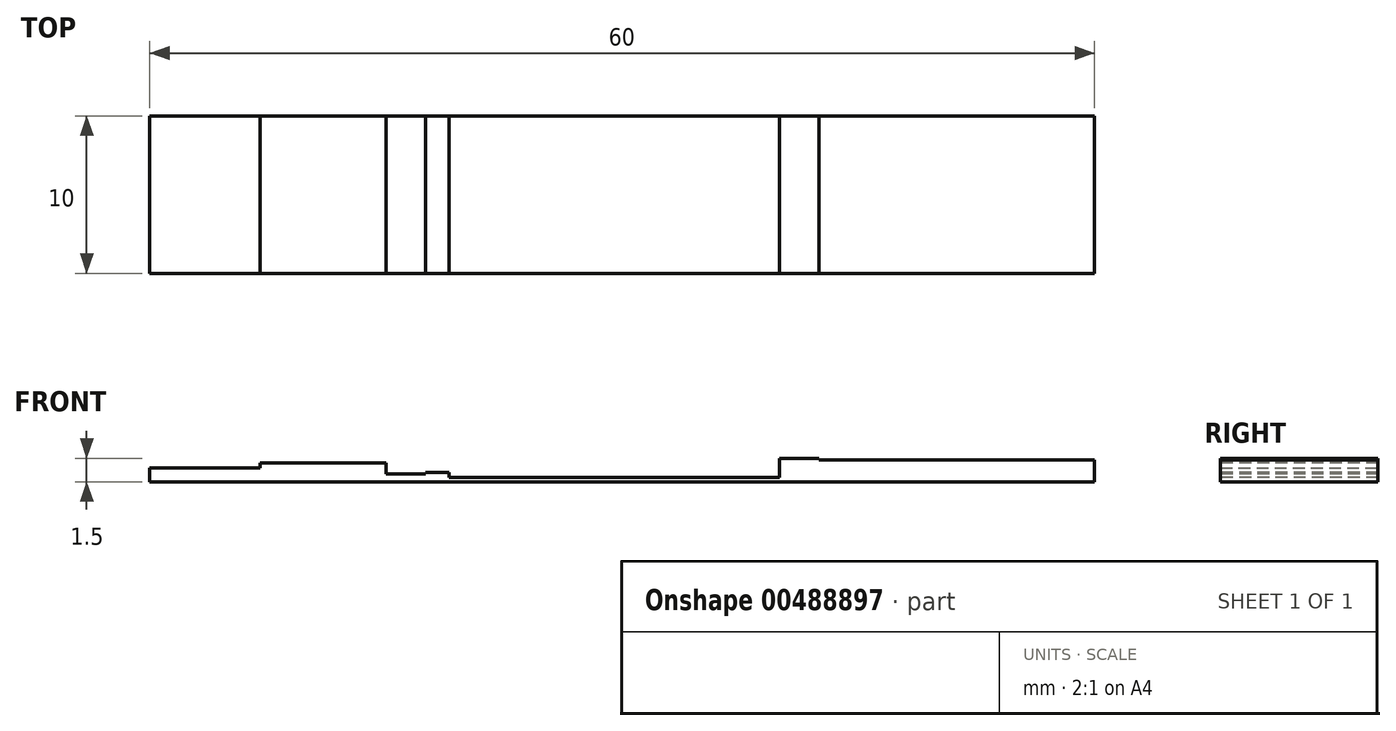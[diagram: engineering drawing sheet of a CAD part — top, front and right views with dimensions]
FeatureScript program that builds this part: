
annotation { "Feature Type Name" : "Feature", "Feature Type Description" : "" }
export const myFeature = defineFeature(function(context is Context, id is Id, definition is map)
    precondition{}
    {
        {
            var Q0;
            Q0=qCreatedBy(makeId("Top.planeOp"),FACE);
            var sketch = newSketch(context, id + "F0", { "sketchPlane" : qUnion([Q0])});
            skLineSegment(sketch, "E0.bottom", {"start": v(30, -5) * mm, "end": v(-30, -5) * mm});
            skLineSegment(sketch, "E0.top", {"start": v(30, 5) * mm, "end": v(-30, 5) * mm});
            skLineSegment(sketch, "E0.left", {"start": v(30, -5) * mm, "end": v(30, 5) * mm});
            skLineSegment(sketch, "E0.right", {"start": v(-30, -5) * mm, "end": v(-30, 5) * mm});
            skPoint(sketch, "E0.middle", {"position": v(0, 0) * mm});
            skSolve(sketch);
        }
        {
            var Q0;
            Q0=makeQuery(id+"F0.imprint","IMPRINT",FACE,{"disambiguationData":[TD([[makeQuery(id+"F0.imprint","IMPRINT",EDGE,{"derivedFrom":sQuery(id+"F0.wireOp",EDGE,"E0.bottom")}),-1.0]])]});
            extrude(context, id + "F1", {"entities" : qUnion([Q0]), "depth" : 0.2 * mm});
        }
        {
            var Q0;
            Q0=makeQuery(id+"F1.opExtrude","CAP_FACE",FACE,{"disambiguationData":[OSD([sQuery(id+"F0.wireOp",EDGE,"E0.bottom"),sQuery(id+"F0.wireOp",EDGE,"E0.top"),sQuery(id+"F0.wireOp",EDGE,"E0.left"),sQuery(id+"F0.wireOp",EDGE,"E0.right")])],"isStart":false});
            var sketch = newSketch(context, id + "F2", { "sketchPlane" : qUnion([Q0])});
            skLineSegment(sketch, "E1.bottom", {"start": v(-12.5, 5) * mm, "end": v(12.5, 5) * mm});
            skLineSegment(sketch, "E1.top", {"start": v(-12.5, -5) * mm, "end": v(12.5, -5) * mm});
            skLineSegment(sketch, "E1.left", {"start": v(-12.5, 5) * mm, "end": v(-12.5, -5) * mm});
            skLineSegment(sketch, "E1.right", {"start": v(12.5, 5) * mm, "end": v(12.5, -5) * mm});
            skSolve(sketch);
        }
        {
            var Q0;
            Q0=makeQuery(id+"F2.imprint","IMPRINT",FACE,{"disambiguationData":[TD([[makeQuery(id+"F2.imprint","IMPRINT",EDGE,{"derivedFrom":sQuery(id+"F2.wireOp",EDGE,"E1.bottom")}),1.0]])]});
            extrude(context, id + "F3", {"entities" : qUnion([Q0]), "operationType" : NewBodyOperationType.ADD, "depth" : 0.1 * mm});
        }
        {
            var Q0;
            Q0=makeQuery(id+"F3.opExtrude","CAP_FACE",FACE,{"disambiguationData":[OSD([sQuery(id+"F2.wireOp",EDGE,"E1.bottom"),sQuery(id+"F2.wireOp",EDGE,"E1.top"),sQuery(id+"F2.wireOp",EDGE,"E1.left"),sQuery(id+"F2.wireOp",EDGE,"E1.right")])],"isStart":false});
            var sketch = newSketch(context, id + "F4", { "sketchPlane" : qUnion([Q0])});
            skLineSegment(sketch, "E2.bottom", {"start": v(-12.5, 5) * mm, "end": v(-11, 5) * mm});
            skLineSegment(sketch, "E2.top", {"start": v(-12.5, -5) * mm, "end": v(-11, -5) * mm});
            skLineSegment(sketch, "E2.left", {"start": v(-12.5, 5) * mm, "end": v(-12.5, -5) * mm});
            skLineSegment(sketch, "E2.right", {"start": v(-11, 5) * mm, "end": v(-11, -5) * mm});
            skSolve(sketch);
        }
        {
            var Q0;
            Q0=makeQuery(id+"F4.imprint","IMPRINT",FACE,{"disambiguationData":[TD([[makeQuery(id+"F4.imprint","IMPRINT",EDGE,{"derivedFrom":sQuery(id+"F4.wireOp",EDGE,"E2.bottom")}),1.0]])]});
            extrude(context, id + "F5", {"entities" : qUnion([Q0]), "operationType" : NewBodyOperationType.ADD, "depth" : 0.3 * mm});
        }
        {
            var Q0;
            {var subQ0=sQuery(id+"F0.wireOp",EDGE,"E0.top");var subQ1=sQuery(id+"F0.wireOp",EDGE,"E0.right");var subQ2=sQuery(id+"F0.wireOp",EDGE,"E0.bottom");Q0=makeQuery(id+"F3.boolean.opBoolean","SPLIT",FACE,{"disambiguationData":[TD([makeQuery(id+"F1.opExtrude","SWEPT_FACE",FACE,{"disambiguationData":[OSD([subQ1])]})])],"derivedFrom":makeQuery(id+"F1.opExtrude","CAP_FACE",FACE,{"disambiguationData":[OSD([subQ2,subQ0,sQuery(id+"F0.wireOp",EDGE,"E0.left"),subQ1])],"isStart":false})});}
            var sketch = newSketch(context, id + "F6", { "sketchPlane" : qUnion([Q0])});
            skLineSegment(sketch, "E3.bottom", {"start": v(-12.5, 5) * mm, "end": v(-23, 5) * mm});
            skLineSegment(sketch, "E3.top", {"start": v(-12.5, -5) * mm, "end": v(-23, -5) * mm});
            skLineSegment(sketch, "E3.left", {"start": v(-12.5, 5) * mm, "end": v(-12.5, -5) * mm});
            skLineSegment(sketch, "E3.right", {"start": v(-23, 5) * mm, "end": v(-23, -5) * mm});
            skSolve(sketch);
        }
        {
            var Q0;
            Q0=makeQuery(id+"F6.imprint","IMPRINT",FACE,{"disambiguationData":[TD([[makeQuery(id+"F6.imprint","IMPRINT",EDGE,{"derivedFrom":sQuery(id+"F6.wireOp",EDGE,"E3.bottom")}),1.0]])]});
            extrude(context, id + "F7", {"entities" : qUnion([Q0]), "operationType" : NewBodyOperationType.ADD, "depth" : 0.3 * mm});
        }
        {
            var Q0;
            {var subQ0=sQuery(id+"F0.wireOp",EDGE,"E0.top");var subQ1=sQuery(id+"F0.wireOp",EDGE,"E0.right");var subQ2=sQuery(id+"F0.wireOp",EDGE,"E0.bottom");Q0=makeQuery(id+"F3.boolean.opBoolean","SPLIT",FACE,{"disambiguationData":[TD([makeQuery(id+"F1.opExtrude","SWEPT_FACE",FACE,{"disambiguationData":[OSD([subQ1])]})])],"derivedFrom":makeQuery(id+"F1.opExtrude","CAP_FACE",FACE,{"disambiguationData":[OSD([subQ2,subQ0,sQuery(id+"F0.wireOp",EDGE,"E0.left"),subQ1])],"isStart":false})});}
            var sketch = newSketch(context, id + "F8", { "sketchPlane" : qUnion([Q0])});
            skLineSegment(sketch, "E4.bottom", {"start": v(-23, 5) * mm, "end": v(-30, 5) * mm});
            skLineSegment(sketch, "E4.top", {"start": v(-23, -5) * mm, "end": v(-30, -5) * mm});
            skLineSegment(sketch, "E4.left", {"start": v(-23, 5) * mm, "end": v(-23, -5) * mm});
            skLineSegment(sketch, "E4.right", {"start": v(-30, 5) * mm, "end": v(-30, -5) * mm});
            skSolve(sketch);
        }
        {
            var Q0;
            Q0=makeQuery(id+"F8.imprint","IMPRINT",FACE,{"disambiguationData":[TD([[makeQuery(id+"F8.imprint","IMPRINT",EDGE,{"derivedFrom":sQuery(id+"F8.wireOp",EDGE,"E4.bottom")}),1.0]])]});
            extrude(context, id + "F9", {"entities" : qUnion([Q0]), "operationType" : NewBodyOperationType.ADD, "depth" : 0.7 * mm});
        }
        {
            var Q0;
            Q0=makeQuery(id+"F7.opExtrude","CAP_FACE",FACE,{"disambiguationData":[OSD([sQuery(id+"F6.wireOp",EDGE,"E3.bottom"),sQuery(id+"F6.wireOp",EDGE,"E3.top"),sQuery(id+"F6.wireOp",EDGE,"E3.left"),sQuery(id+"F6.wireOp",EDGE,"E3.right")])],"isStart":false});
            var sketch = newSketch(context, id + "F10", { "sketchPlane" : qUnion([Q0])});
            skLineSegment(sketch, "E5.bottom", {"start": v(-23, 5) * mm, "end": v(-15, 5) * mm});
            skLineSegment(sketch, "E5.top", {"start": v(-23, -5) * mm, "end": v(-15, -5) * mm});
            skLineSegment(sketch, "E5.left", {"start": v(-23, 5) * mm, "end": v(-23, -5) * mm});
            skLineSegment(sketch, "E5.right", {"start": v(-15, 5) * mm, "end": v(-15, -5) * mm});
            skSolve(sketch);
        }
        {
            var Q0;
            Q0=makeQuery(id+"F10.imprint","IMPRINT",FACE,{"disambiguationData":[TD([[makeQuery(id+"F10.imprint","IMPRINT",EDGE,{"derivedFrom":sQuery(id+"F10.wireOp",EDGE,"E5.bottom")}),1.0]])]});
            extrude(context, id + "F11", {"entities" : qUnion([Q0]), "operationType" : NewBodyOperationType.ADD, "depth" : 0.7 * mm});
        }
        {
            var Q0;
            {var subQ0=sQuery(id+"F0.wireOp",EDGE,"E0.left");var subQ1=sQuery(id+"F0.wireOp",EDGE,"E0.top");var subQ2=sQuery(id+"F0.wireOp",EDGE,"E0.bottom");Q0=makeQuery(id+"F3.boolean.opBoolean","SPLIT",FACE,{"disambiguationData":[TD([makeQuery(id+"F1.opExtrude","SWEPT_FACE",FACE,{"disambiguationData":[OSD([subQ0])]})])],"derivedFrom":makeQuery(id+"F1.opExtrude","CAP_FACE",FACE,{"disambiguationData":[OSD([subQ2,subQ1,subQ0,sQuery(id+"F0.wireOp",EDGE,"E0.right")])],"isStart":false})});}
            var sketch = newSketch(context, id + "F12", { "sketchPlane" : qUnion([Q0])});
            skLineSegment(sketch, "E6.bottom", {"start": v(12.5, 5) * mm, "end": v(30, 5) * mm});
            skLineSegment(sketch, "E6.top", {"start": v(12.5, -5) * mm, "end": v(30, -5) * mm});
            skLineSegment(sketch, "E6.left", {"start": v(12.5, 5) * mm, "end": v(12.5, -5) * mm});
            skLineSegment(sketch, "E6.right", {"start": v(30, 5) * mm, "end": v(30, -5) * mm});
            skSolve(sketch);
        }
        {
            var Q0;
            Q0=makeQuery(id+"F12.imprint","IMPRINT",FACE,{"disambiguationData":[TD([[makeQuery(id+"F12.imprint","IMPRINT",EDGE,{"derivedFrom":sQuery(id+"F12.wireOp",EDGE,"E6.bottom")}),1.0]])]});
            extrude(context, id + "F13", {"entities" : qUnion([Q0]), "operationType" : NewBodyOperationType.ADD, "depth" : 1.2 * mm});
        }
        {
            var Q0;
            Q0=makeQuery(id+"F3.opExtrude","CAP_FACE",FACE,{"disambiguationData":[OSD([sQuery(id+"F2.wireOp",EDGE,"E1.bottom"),sQuery(id+"F2.wireOp",EDGE,"E1.top"),sQuery(id+"F2.wireOp",EDGE,"E1.left"),sQuery(id+"F2.wireOp",EDGE,"E1.right")])],"isStart":false});
            var sketch = newSketch(context, id + "F14", { "sketchPlane" : qUnion([Q0])});
            skLineSegment(sketch, "E7.bottom", {"start": v(12.5, 5) * mm, "end": v(10, 5) * mm});
            skLineSegment(sketch, "E7.top", {"start": v(12.5, -5) * mm, "end": v(10, -5) * mm});
            skLineSegment(sketch, "E7.left", {"start": v(12.5, 5) * mm, "end": v(12.5, -5) * mm});
            skLineSegment(sketch, "E7.right", {"start": v(10, 5) * mm, "end": v(10, -5) * mm});
            skSolve(sketch);
        }
        {
            var Q0;
            Q0=makeQuery(id+"F14.imprint","IMPRINT",FACE,{"disambiguationData":[TD([[makeQuery(id+"F14.imprint","IMPRINT",EDGE,{"derivedFrom":sQuery(id+"F14.wireOp",EDGE,"E7.bottom")}),1.0]])]});
            extrude(context, id + "F15", {"entities" : qUnion([Q0]), "operationType" : NewBodyOperationType.ADD, "depth" : 1.2 * mm});
        }
    });
